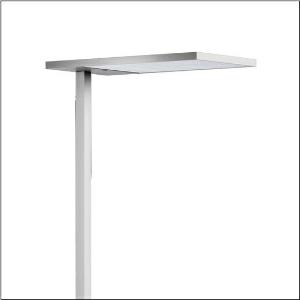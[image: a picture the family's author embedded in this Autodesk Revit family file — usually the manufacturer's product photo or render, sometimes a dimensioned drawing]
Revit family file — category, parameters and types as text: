
# Revit family: silica_r__21_floor_r_51mx53sg4ds_70f9
name_source: partatom
category: Lighting Fixtures
units: mm (PartAtom-declared; Revit-internal decimal feet)

## family parameters
Cut with Voids When Loaded = No
Host = Face
Light Source = No
Part Type = Normal
Room Calculation Point = No
Round Connector Dimension = Use Diameter
Shared = No

## types (1)
- Silica® 21 Floor R (1 x LED, 15000 lm, 106.4 W, 4000K)
    Apparent Load = 106 VA
    CIE Flux Codes = 54 86 97 13 100
    Color Rendering = 80
    Color Temperature = 4000K
    Default Elevation = 1800 mm
    Description = Silica® 21 Floor R, floorstanding luminaire, of PMMA, primary optical cover: prismatic diffuser, of PMMA, CAT 2 (L<= 3000cd/m²), light emission: indirect/direct distribution, primary light characteristic: symmetric, installation type: not mounted, LED, rated luminous flux: 15.000lm, luminous efficacy: 141lm/W, light colour: 840, colour temperature: 4000K, control gear: ECG DALI, daylight-dependent control, mains connection: 230V, 50Hz, connection cable pre-assembled, cable length: 2,5m, rated input power: 106.4W, luminaire head, of aluminium, metallic grey (RAL 9006), length: 650mm, width: 350mm, supporting column, angular, of aluminium, metallic grey (RAL 9006), baseplate, of steel, metallic grey (RAL 9006), protection rating (complete): IP20, insulation class (complete): insulation class I (protective earthing), certification: CE, standard: EN 50419, packaging unit: 1 piece
    Height = 18 mm
    Lamp = 1 x LED
    Lamp Light Flux = 15000 lm
    Lamp Power = 106.4 W
    Lamp count = 1
    Length = 650 mm
    Luminous efficacy = 141 lm/W
    Manufacturer = Siteco
    ModVariant = No
    Model = 51MX53SG4DS
    Mounting Place = Floor
    Mounting Type = Freestanding
    Number of Poles = 1
    OnlyDefault = Yes
    Power Factor = 1
    Product Name = Silica® 21 Floor R
    Product group = floorstanding luminaire
    ProductGroupID = 1301
    Protection Class = Protection class I
    Protection Degree = IP 20
    RLX_Detail_Level = 1
    RLX_Emergency_Light_Flux = 0 lm
    RLX_Emergency_Type = 0
    RLX_Emergency_Type_DB = No
    RlxData = <blob elided: 20209 chars, md5=fdedf381>
    Socket = socket
    Standby Power = 0 W
    System Light Flux = 15000 lm
    System Power = 106 W
    Type Comments = Product without accessories
    Type Image = l_1006716.jpg
    URL = http://relux.com
    VarID = ---
    Voltage = 0 V
    Weight = 0.00 kg
    Width = 350 mm

## geometry (parser evidence)
native form markers: Blend x4, Sweep x16
no freeform markers — native parametric forms only
